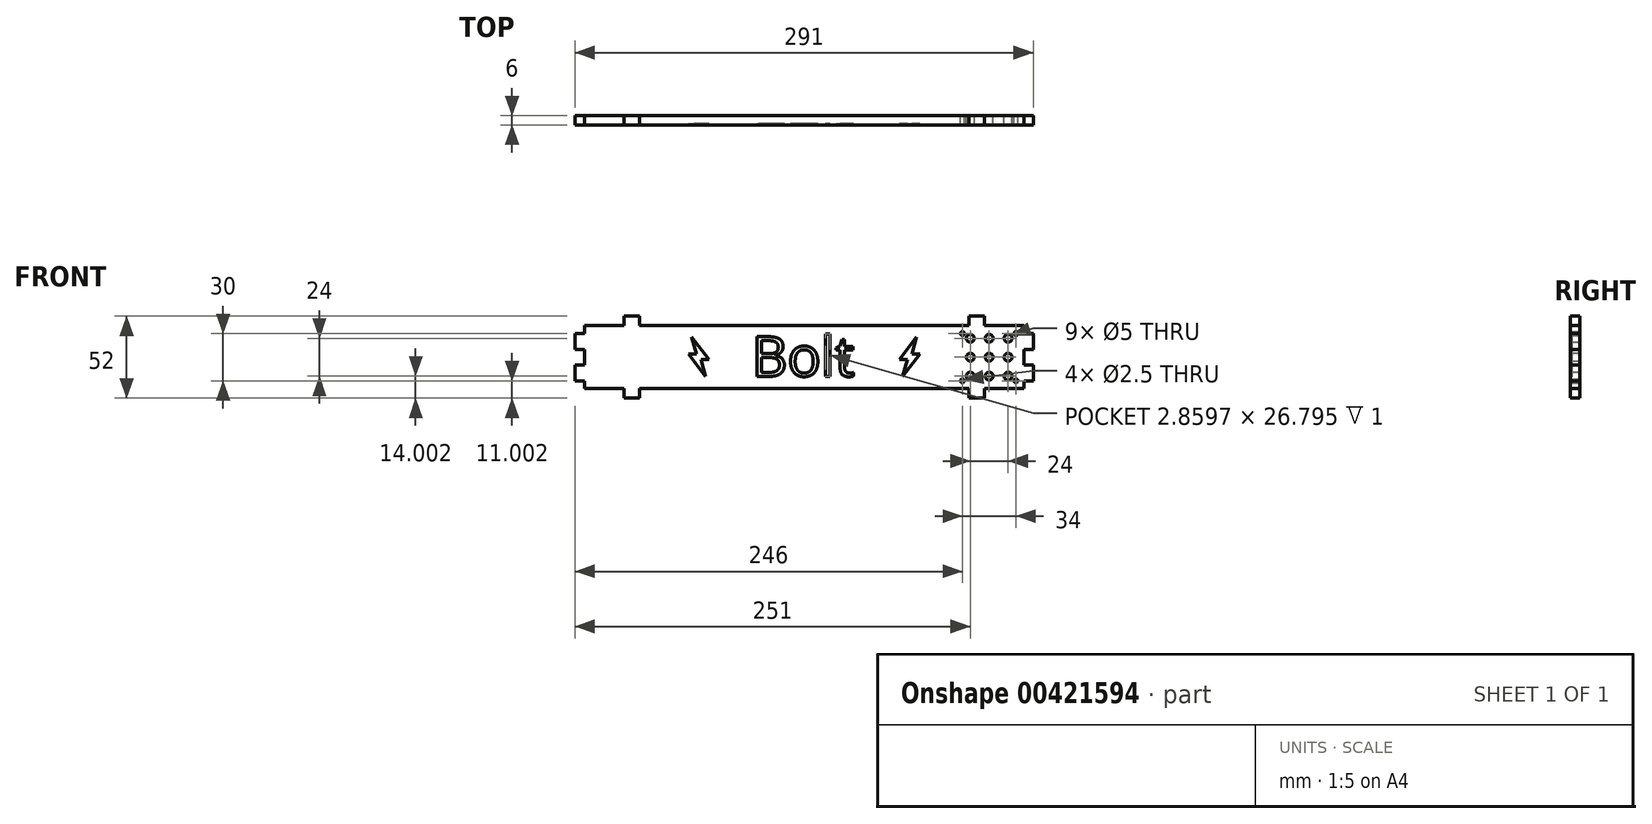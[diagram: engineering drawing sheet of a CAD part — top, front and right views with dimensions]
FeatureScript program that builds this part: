
annotation { "Feature Type Name" : "Feature", "Feature Type Description" : "" }
export const myFeature = defineFeature(function(context is Context, id is Id, definition is map)
    precondition{}
    {
        {
            var Q0;
            Q0=qCreatedBy(makeId("Front.planeOp"),FACE);
            var sketch = newSketch(context, id + "F0", { "sketchPlane" : qUnion([Q0])});
            skLineSegment(sketch, "E0", {"start": v(-139.5, -68.53) * mm, "end": v(-114.5, -68.53) * mm});
            skLineSegment(sketch, "E1", {"start": v(-104.5, -74.53) * mm, "end": v(-104.5, -68.53) * mm});
            skLineSegment(sketch, "E2.MirrorCS", {"start": v(-139.5, -28.53) * mm, "end": v(-114.5, -28.53) * mm});
            skLineSegment(sketch, "E3.MirrorCS", {"start": v(-139.5, -33.53) * mm, "end": v(-139.5, -28.53) * mm});
            skLineSegment(sketch, "E4.MirrorCS", {"start": v(-139.5, -43.53) * mm, "end": v(-145.5, -43.53) * mm});
            skLineSegment(sketch, "E5.MirrorCS", {"start": v(-139.5, -53.53) * mm, "end": v(-139.5, -43.53) * mm});
            skLineSegment(sketch, "E6", {"start": v(-139.5, -68.53) * mm, "end": v(-139.5, -63.53) * mm});
            skLineSegment(sketch, "E7", {"start": v(-139.5, -63.53) * mm, "end": v(-145.5, -63.53) * mm});
            skLineSegment(sketch, "E8", {"start": v(-104.5, -68.53) * mm, "end": v(0, -68.53) * mm});
            skLineSegment(sketch, "E9", {"start": v(-104.5, -22.53) * mm, "end": v(-104.5, -28.53) * mm});
            skLineSegment(sketch, "E10", {"start": v(-104.5, -28.53) * mm, "end": v(0, -28.53) * mm});
            skLineSegment(sketch, "E11.MirrorCS", {"start": v(104.5, -68.53) * mm, "end": v(0, -68.53) * mm});
            skLineSegment(sketch, "E12.MirrorCS", {"start": v(104.5, -74.53) * mm, "end": v(104.5, -68.53) * mm});
            skLineSegment(sketch, "E13.MirrorCS", {"start": v(104.5, -28.53) * mm, "end": v(0, -28.53) * mm});
            skLineSegment(sketch, "E14.MirrorCS", {"start": v(139.5, -63.53) * mm, "end": v(145.5, -63.53) * mm});
            skLineSegment(sketch, "E15.MirrorCS", {"start": v(139.5, -28.53) * mm, "end": v(114.5, -28.53) * mm});
            skLineSegment(sketch, "E16.MirrorCS", {"start": v(139.5, -68.53) * mm, "end": v(114.5, -68.53) * mm});
            skLineSegment(sketch, "E17.MirrorCS", {"start": v(104.5, -22.53) * mm, "end": v(104.5, -28.53) * mm});
            skLineSegment(sketch, "E18.MirrorCS", {"start": v(139.5, -33.53) * mm, "end": v(139.5, -28.53) * mm});
            skLineSegment(sketch, "E19.MirrorCS", {"start": v(139.5, -43.53) * mm, "end": v(145.5, -43.53) * mm});
            skLineSegment(sketch, "E20.MirrorCS", {"start": v(139.5, -53.53) * mm, "end": v(139.5, -43.53) * mm});
            skLineSegment(sketch, "E21.MirrorCS", {"start": v(139.5, -68.53) * mm, "end": v(139.5, -63.53) * mm});
            skCircle(sketch, "E22", {"center": v(105.5, -36.53) * mm, "radius": 2.5 * mm});
            skCircle(sketch, "E23", {"center": v(117.5, -36.53) * mm, "radius": 2.5 * mm});
            skCircle(sketch, "E24", {"center": v(129.5, -36.53) * mm, "radius": 2.5 * mm});
            skCircle(sketch, "E25", {"center": v(105.5, -48.53) * mm, "radius": 2.5 * mm});
            skCircle(sketch, "E26", {"center": v(117.5, -48.53) * mm, "radius": 2.5 * mm});
            skCircle(sketch, "E27", {"center": v(129.5, -48.53) * mm, "radius": 2.5 * mm});
            skCircle(sketch, "E28", {"center": v(105.5, -60.53) * mm, "radius": 2.5 * mm});
            skCircle(sketch, "E29", {"center": v(117.5, -60.53) * mm, "radius": 2.5 * mm});
            skCircle(sketch, "E30", {"center": v(129.5, -60.53) * mm, "radius": 2.5 * mm});
            skCircle(sketch, "E31", {"center": v(100.5, -33.53) * mm, "radius": 1.25 * mm});
            skCircle(sketch, "E32.MirrorC", {"center": v(100.5, -63.53) * mm, "radius": 1.25 * mm});
            skCircle(sketch, "E33.MirrorC", {"center": v(134.5, -63.53) * mm, "radius": 1.25 * mm});
            skCircle(sketch, "E34.MirrorC", {"center": v(134.5, -33.53) * mm, "radius": 1.25 * mm});
            skLineSegment(sketch, "E35", {"start": v(-104.5, -22.53) * mm, "end": v(-114.5, -22.53) * mm});
            skLineSegment(sketch, "E36", {"start": v(-114.5, -22.53) * mm, "end": v(-114.5, -28.53) * mm});
            skLineSegment(sketch, "E37", {"start": v(-104.5, -74.53) * mm, "end": v(-114.5, -74.53) * mm});
            skLineSegment(sketch, "E38", {"start": v(-114.5, -74.53) * mm, "end": v(-114.5, -68.53) * mm});
            skLineSegment(sketch, "E39", {"start": v(-145.5, -63.53) * mm, "end": v(-145.5, -53.53) * mm});
            skLineSegment(sketch, "E40", {"start": v(-145.5, -53.53) * mm, "end": v(-139.5, -53.53) * mm});
            skLineSegment(sketch, "E41", {"start": v(-145.5, -43.53) * mm, "end": v(-145.5, -33.53) * mm});
            skLineSegment(sketch, "E42", {"start": v(-145.5, -33.53) * mm, "end": v(-139.5, -33.53) * mm});
            skLineSegment(sketch, "E43.MirrorCS", {"start": v(104.5, -22.53) * mm, "end": v(114.5, -22.53) * mm});
            skLineSegment(sketch, "E44.MirrorCS", {"start": v(114.5, -22.53) * mm, "end": v(114.5, -28.53) * mm});
            skLineSegment(sketch, "E45.MirrorCS", {"start": v(145.5, -33.53) * mm, "end": v(139.5, -33.53) * mm});
            skLineSegment(sketch, "E46.MirrorCS", {"start": v(145.5, -43.53) * mm, "end": v(145.5, -33.53) * mm});
            skLineSegment(sketch, "E47.MirrorCS", {"start": v(145.5, -63.53) * mm, "end": v(145.5, -53.53) * mm});
            skLineSegment(sketch, "E48.MirrorCS", {"start": v(104.5, -74.53) * mm, "end": v(114.5, -74.53) * mm});
            skLineSegment(sketch, "E49.MirrorCS", {"start": v(114.5, -74.53) * mm, "end": v(114.5, -68.53) * mm});
            skLineSegment(sketch, "E50.MirrorCS", {"start": v(145.5, -53.53) * mm, "end": v(139.5, -53.53) * mm});
            skSolve(sketch);
        }
        {
            var Q0;
            Q0=makeQuery(id+"F0.imprint","IMPRINT",FACE,{"disambiguationData":[TD([[makeQuery(id+"F0.imprint","IMPRINT",EDGE,{"derivedFrom":sQuery(id+"F0.wireOp",EDGE,"E0")}),1.0]])]});
            var Q1;
            Q1=makeQuery(id+"F0.imprint","IMPRINT",FACE,{"disambiguationData":[TD([[makeQuery(id+"F0.imprint","IMPRINT",EDGE,{"derivedFrom":sQuery(id+"F0.wireOp",EDGE,"1bf84472-e018-454b-94ab-7f4b09c15b33.sketch_text.stroke-18")}),1.0]])]});
            var Q2;
            Q2=makeQuery(id+"F0.imprint","IMPRINT",FACE,{"disambiguationData":[TD([[makeQuery(id+"F0.imprint","IMPRINT",EDGE,{"derivedFrom":sQuery(id+"F0.wireOp",EDGE,"1bf84472-e018-454b-94ab-7f4b09c15b33.sketch_text.stroke-11")}),1.0]])]});
            var Q3;
            Q3=makeQuery(id+"F0.imprint","IMPRINT",FACE,{"disambiguationData":[TD([[makeQuery(id+"F0.imprint","IMPRINT",EDGE,{"derivedFrom":sQuery(id+"F0.wireOp",EDGE,"1bf84472-e018-454b-94ab-7f4b09c15b33.sketch_text.stroke-34")}),1.0]])]});
            var Q4;
            Q4=makeQuery(id+"F0.imprint","IMPRINT",FACE,{"disambiguationData":[TD([[makeQuery(id+"F0.imprint","IMPRINT",EDGE,{"derivedFrom":sQuery(id+"F0.wireOp",EDGE,"1bf84472-e018-454b-94ab-7f4b09c15b33.sketch_text.stroke-46")}),-1.0]])]});
            var Q5;
            Q5=makeQuery(id+"F0.imprint","IMPRINT",FACE,{"disambiguationData":[TD([[makeQuery(id+"F0.imprint","IMPRINT",EDGE,{"derivedFrom":sQuery(id+"F0.wireOp",EDGE,"1bf84472-e018-454b-94ab-7f4b09c15b33.sketch_text.stroke-42")}),-1.0]])]});
            var Q6;
            Q6=makeQuery(id+"F0.imprint","IMPRINT",FACE,{"disambiguationData":[TD([[makeQuery(id+"F0.imprint","IMPRINT",EDGE,{"derivedFrom":sQuery(id+"F0.wireOp",EDGE,"1bf84472-e018-454b-94ab-7f4b09c15b33.sketch_text.stroke-25")}),-1.0]])]});
            var Q7;
            Q7=makeQuery(id+"F0.imprint","IMPRINT",FACE,{"disambiguationData":[TD([[makeQuery(id+"F0.imprint","IMPRINT",EDGE,{"derivedFrom":sQuery(id+"F0.wireOp",EDGE,"1bf84472-e018-454b-94ab-7f4b09c15b33.sketch_text.stroke-0")}),-1.0]])]});
            var Q8;
            Q8=makeQuery(id+"F0.imprint","IMPRINT",FACE,{"disambiguationData":[TD([[makeQuery(id+"F0.imprint","IMPRINT",EDGE,{"derivedFrom":sQuery(id+"F0.wireOp",EDGE,"1de8859a-47fc-4e15-9f36-81b63d15cdb2.sketch_text.stroke-0")}),-1.0]])]});
            var Q9;
            Q9=makeQuery(id+"F0.imprint","IMPRINT",FACE,{"disambiguationData":[TD([[makeQuery(id+"F0.imprint","IMPRINT",EDGE,{"derivedFrom":sQuery(id+"F0.wireOp",EDGE,"1de8859a-47fc-4e15-9f36-81b63d15cdb2.sketch_text.stroke-11")}),1.0]])]});
            var Q10;
            Q10=makeQuery(id+"F0.imprint","IMPRINT",FACE,{"disambiguationData":[TD([[makeQuery(id+"F0.imprint","IMPRINT",EDGE,{"derivedFrom":sQuery(id+"F0.wireOp",EDGE,"1de8859a-47fc-4e15-9f36-81b63d15cdb2.sketch_text.stroke-18")}),1.0]])]});
            var Q11;
            Q11=makeQuery(id+"F0.imprint","IMPRINT",FACE,{"disambiguationData":[TD([[makeQuery(id+"F0.imprint","IMPRINT",EDGE,{"derivedFrom":sQuery(id+"F0.wireOp",EDGE,"1de8859a-47fc-4e15-9f36-81b63d15cdb2.sketch_text.stroke-42")}),-1.0]])]});
            var Q12;
            Q12=makeQuery(id+"F0.imprint","IMPRINT",FACE,{"disambiguationData":[TD([[makeQuery(id+"F0.imprint","IMPRINT",EDGE,{"derivedFrom":sQuery(id+"F0.wireOp",EDGE,"1de8859a-47fc-4e15-9f36-81b63d15cdb2.sketch_text.stroke-46")}),-1.0]])]});
            var Q13;
            Q13=makeQuery(id+"F0.imprint","IMPRINT",FACE,{"disambiguationData":[TD([[makeQuery(id+"F0.imprint","IMPRINT",EDGE,{"derivedFrom":sQuery(id+"F0.wireOp",EDGE,"1de8859a-47fc-4e15-9f36-81b63d15cdb2.sketch_text.stroke-34")}),1.0]])]});
            var Q14;
            Q14=makeQuery(id+"F0.imprint","IMPRINT",FACE,{"disambiguationData":[TD([[makeQuery(id+"F0.imprint","IMPRINT",EDGE,{"derivedFrom":sQuery(id+"F0.wireOp",EDGE,"1de8859a-47fc-4e15-9f36-81b63d15cdb2.sketch_text.stroke-25")}),-1.0]])]});
            var Q15;
            Q15=makeQuery(id+"F0.imprint","IMPRINT",FACE,{"disambiguationData":[TD([[makeQuery(id+"F0.imprint","IMPRINT",EDGE,{"derivedFrom":sQuery(id+"F0.wireOp",EDGE,"076e43a0-6d1f-4a10-992f-eacb876b981b.sketch_text.stroke-11")}),1.0]])]});
            var Q16;
            Q16=makeQuery(id+"F0.imprint","IMPRINT",FACE,{"disambiguationData":[TD([[makeQuery(id+"F0.imprint","IMPRINT",EDGE,{"derivedFrom":sQuery(id+"F0.wireOp",EDGE,"076e43a0-6d1f-4a10-992f-eacb876b981b.sketch_text.stroke-0")}),-1.0]])]});
            var Q17;
            Q17=makeQuery(id+"F0.imprint","IMPRINT",FACE,{"disambiguationData":[TD([[makeQuery(id+"F0.imprint","IMPRINT",EDGE,{"derivedFrom":sQuery(id+"F0.wireOp",EDGE,"076e43a0-6d1f-4a10-992f-eacb876b981b.sketch_text.stroke-18")}),1.0]])]});
            var Q18;
            Q18=makeQuery(id+"F0.imprint","IMPRINT",FACE,{"disambiguationData":[TD([[makeQuery(id+"F0.imprint","IMPRINT",EDGE,{"derivedFrom":sQuery(id+"F0.wireOp",EDGE,"076e43a0-6d1f-4a10-992f-eacb876b981b.sketch_text.stroke-34")}),1.0]])]});
            var Q19;
            Q19=makeQuery(id+"F0.imprint","IMPRINT",FACE,{"disambiguationData":[TD([[makeQuery(id+"F0.imprint","IMPRINT",EDGE,{"derivedFrom":sQuery(id+"F0.wireOp",EDGE,"076e43a0-6d1f-4a10-992f-eacb876b981b.sketch_text.stroke-25")}),-1.0]])]});
            var Q20;
            Q20=makeQuery(id+"F0.imprint","IMPRINT",FACE,{"disambiguationData":[TD([[makeQuery(id+"F0.imprint","IMPRINT",EDGE,{"derivedFrom":sQuery(id+"F0.wireOp",EDGE,"076e43a0-6d1f-4a10-992f-eacb876b981b.sketch_text.stroke-42")}),-1.0]])]});
            var Q21;
            Q21=makeQuery(id+"F0.imprint","IMPRINT",FACE,{"disambiguationData":[TD([[makeQuery(id+"F0.imprint","IMPRINT",EDGE,{"derivedFrom":sQuery(id+"F0.wireOp",EDGE,"076e43a0-6d1f-4a10-992f-eacb876b981b.sketch_text.stroke-46")}),-1.0]])]});
            extrude(context, id + "F1", {"entities" : qUnion([Q0, Q1, Q2, Q3, Q4, Q5, Q6, Q7, Q8, Q9, Q10, Q11, Q12, Q13, Q14, Q15, Q16, Q17, Q18, Q19, Q20, Q21]), "depth" : 6 * mm, "offsetDistance" : 25 * mm});
        }
        {
            var Q0;
            Q0=makeQuery(id+"F1.opExtrude","CAP_FACE",FACE,{"disambiguationData":[OSD([sQuery(id+"F0.wireOp",EDGE,"E0"),sQuery(id+"F0.wireOp",EDGE,"ac5Lo3Xd-x58u-lC21-kUfO-QtuLJ14oxCLl"),sQuery(id+"F0.wireOp",EDGE,"E1"),sQuery(id+"F0.wireOp",EDGE,"E2.MirrorCS"),sQuery(id+"F0.wireOp",EDGE,"7663e152-af19-4a35-83a4-3ea347ceabe70.MirrorCS"),sQuery(id+"F0.wireOp",EDGE,"E3.MirrorCS"),sQuery(id+"F0.wireOp",EDGE,"1624e850-8d91-472c-ae12-f973a9bd839c0.MirrorCS"),sQuery(id+"F0.wireOp",EDGE,"E4.MirrorCS"),sQuery(id+"F0.wireOp",EDGE,"E5.MirrorCS"),sQuery(id+"F0.wireOp",EDGE,"a271d2a8-6993-4264-90ec-e6eb90cab1de0.MirrorCS"),sQuery(id+"F0.wireOp",EDGE,"5WBElvhD-uZn2-3jpI-vGce-8jeJ09ldFoat"),sQuery(id+"F0.wireOp",EDGE,"JQk1ujXt-zTFC-Q9vv-MM2F-JObCWqsVMeTT"),sQuery(id+"F0.wireOp",EDGE,"X4aptTxq-uVn2-vk3P-uYmP-l7kkbDqpvu9T"),sQuery(id+"F0.wireOp",EDGE,"E6"),sQuery(id+"F0.wireOp",EDGE,"E7"),sQuery(id+"F0.wireOp",EDGE,"9kLejEAr-DaZA-wUvd-fjBy-tgoBi6lp2kKG"),sQuery(id+"F0.wireOp",EDGE,"E8"),sQuery(id+"F0.wireOp",EDGE,"E9"),sQuery(id+"F0.wireOp",EDGE,"E10"),sQuery(id+"F0.wireOp",EDGE,"E11.MirrorCS"),sQuery(id+"F0.wireOp",EDGE,"E12.MirrorCS"),sQuery(id+"F0.wireOp",EDGE,"cb20766f-49a6-4d89-ae77-f212504f18da2.MirrorCS"),sQuery(id+"F0.wireOp",EDGE,"cb20766f-49a6-4d89-ae77-f212504f18da3.MirrorCS"),sQuery(id+"F0.wireOp",EDGE,"cb20766f-49a6-4d89-ae77-f212504f18da4.MirrorCS"),sQuery(id+"F0.wireOp",EDGE,"E13.MirrorCS"),sQuery(id+"F0.wireOp",EDGE,"E14.MirrorCS"),sQuery(id+"F0.wireOp",EDGE,"E15.MirrorCS"),sQuery(id+"F0.wireOp",EDGE,"E16.MirrorCS"),sQuery(id+"F0.wireOp",EDGE,"E17.MirrorCS"),sQuery(id+"F0.wireOp",EDGE,"E120.MirrorCS"),sQuery(id+"F0.wireOp",EDGE,"E121.MirrorCS"),sQuery(id+"F0.wireOp",EDGE,"E122.MirrorCS"),sQuery(id+"F0.wireOp",EDGE,"E123.MirrorCS"),sQuery(id+"F0.wireOp",EDGE,"E18.MirrorCS"),sQuery(id+"F0.wireOp",EDGE,"E125.MirrorCS"),sQuery(id+"F0.wireOp",EDGE,"E19.MirrorCS"),sQuery(id+"F0.wireOp",EDGE,"E20.MirrorCS"),sQuery(id+"F0.wireOp",EDGE,"E21.MirrorCS")])],"isStart":false});
            cPlane(context, id + "F2", {"entities" : qUnion([Q0]), "cplaneType" : CPlaneType.OFFSET, "offset" : 0 * mm, "width" : 150 * mm, "height" : 150 * mm});
        }
        {
            var Q0;
            Q0=qCreatedBy(id+"F2.planeOp",FACE);
            var sketch = newSketch(context, id + "F3", { "sketchPlane" : qUnion([Q0])});
            skText(sketch, "E51", { "text": "Bolt", "fontName": "OpenSans-Regular.ttf"});
            skLineSegment(sketch, "E52", {"start": v(62.57, -60.68) * mm, "end": v(73.53, -46.4) * mm});
            skLineSegment(sketch, "E53", {"start": v(73.53, -46.4) * mm, "end": v(68.53, -46.4) * mm});
            skLineSegment(sketch, "E54", {"start": v(62.57, -60.68) * mm, "end": v(65.46, -50.06) * mm});
            skLineSegment(sketch, "E55", {"start": v(65.46, -50.06) * mm, "end": v(60.46, -50.06) * mm});
            skLineSegment(sketch, "E56", {"start": v(60.46, -50.06) * mm, "end": v(71.42, -35.78) * mm});
            skLineSegment(sketch, "E57", {"start": v(71.42, -35.78) * mm, "end": v(68.53, -46.4) * mm});
            skLineSegment(sketch, "E58.MirrorCS", {"start": v(-71.42, -35.78) * mm, "end": v(-68.53, -46.4) * mm});
            skLineSegment(sketch, "E59.MirrorCS", {"start": v(-60.46, -50.06) * mm, "end": v(-71.42, -35.78) * mm});
            skLineSegment(sketch, "E60.MirrorCS", {"start": v(-62.57, -60.68) * mm, "end": v(-73.53, -46.4) * mm});
            skLineSegment(sketch, "E61.MirrorCS", {"start": v(-73.53, -46.4) * mm, "end": v(-68.53, -46.4) * mm});
            skLineSegment(sketch, "E62.MirrorCS", {"start": v(-65.46, -50.06) * mm, "end": v(-60.46, -50.06) * mm});
            skLineSegment(sketch, "E63.MirrorCS", {"start": v(-62.57, -60.68) * mm, "end": v(-65.46, -50.06) * mm});
            const initialGuessF3  = {"E51": [-0.0335, -0.06068, 1, 0, 0.02539]};
            skSetInitialGuess(sketch, initialGuessF3);
            skSolve(sketch);
        }
        {
            var Q0;
            Q0 = qSketchRegion(id + "F3", true);
            extrude(context, id + "F4", {"entities" : qUnion([Q0]), "operationType" : NewBodyOperationType.REMOVE, "oppositeDirection" : true, "depth" : 1 * mm, "offsetDistance" : 25 * mm});
        }
    });
